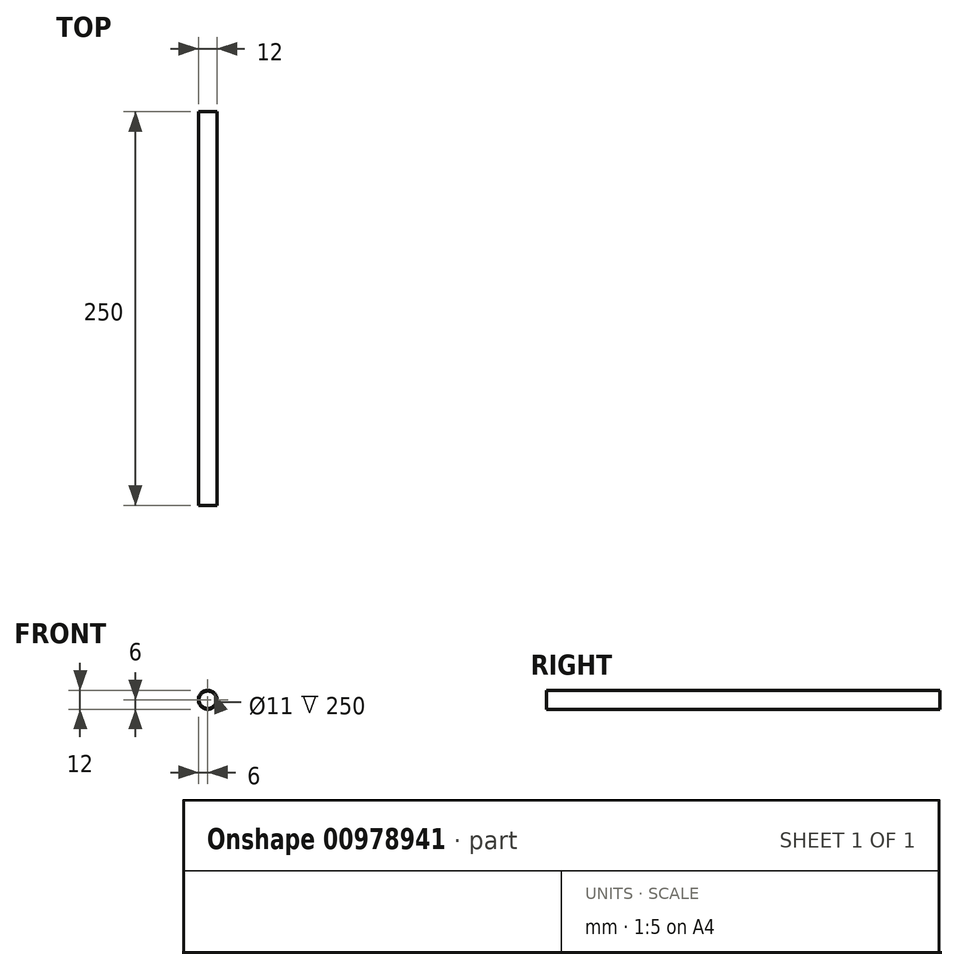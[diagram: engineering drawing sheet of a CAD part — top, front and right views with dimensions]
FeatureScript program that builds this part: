
annotation { "Feature Type Name" : "Feature", "Feature Type Description" : "" }
export const myFeature = defineFeature(function(context is Context, id is Id, definition is map)
    precondition{}
    {
        {
            var Q0;
            Q0=qCreatedBy(makeId("Front.planeOp"),FACE);
            var sketch = newSketch(context, id + "F0", { "sketchPlane" : qUnion([Q0])});
            skCircle(sketch, "E0", {"center": v(0, 0) * mm, "radius": 6 * mm});
            skCircle(sketch, "E1", {"center": v(0, 0) * mm, "radius": 5.5 * mm});
            skSolve(sketch);
        }
        {
            var Q0;
            Q0=makeQuery(id+"F0.imprint","IMPRINT",FACE,{"disambiguationData":[TD([[makeQuery(id+"F0.imprint","IMPRINT",EDGE,{"derivedFrom":sQuery(id+"F0.wireOp",EDGE,"E0")}),1.0]])]});
            extrude(context, id + "F1", {"entities" : qUnion([Q0]), "depth" : 250 * mm, "offsetDistance" : 25 * mm});
        }
    });
